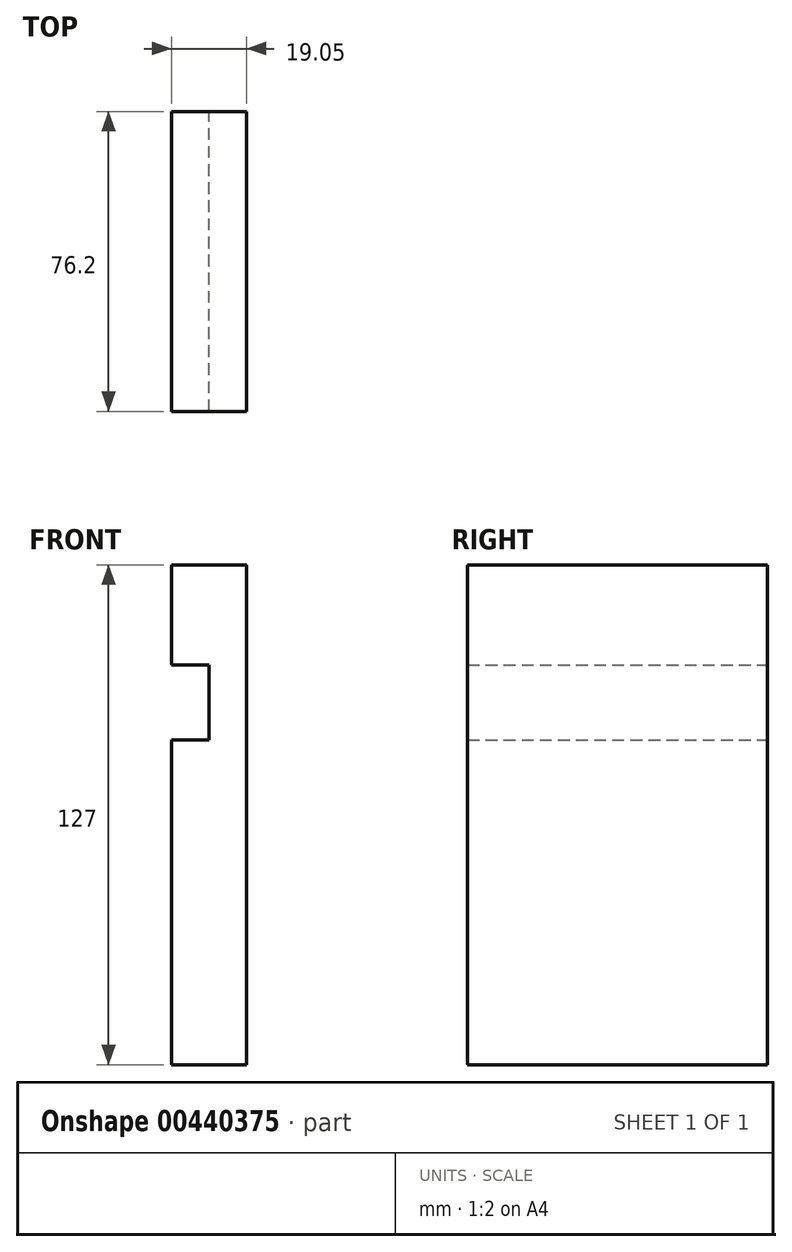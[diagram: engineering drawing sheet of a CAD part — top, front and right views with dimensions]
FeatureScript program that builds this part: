
annotation { "Feature Type Name" : "Feature", "Feature Type Description" : "" }
export const myFeature = defineFeature(function(context is Context, id is Id, definition is map)
    precondition{}
    {
        {
            var Q0;
            Q0=qCreatedBy(makeId("Front.planeOp"),FACE);
            var sketch = newSketch(context, id + "F0", { "sketchPlane" : qUnion([Q0])});
            skLineSegment(sketch, "E0", {"start": v(-28.86, 34.68) * mm, "end": v(-28.86, 161.68) * mm});
            skLineSegment(sketch, "E1", {"start": v(-28.86, 161.68) * mm, "end": v(-47.91, 161.68) * mm});
            skLineSegment(sketch, "E2", {"start": v(-47.91, 161.68) * mm, "end": v(-47.91, 136.28) * mm});
            skLineSegment(sketch, "E3", {"start": v(-47.91, 136.28) * mm, "end": v(-38.39, 136.28) * mm});
            skLineSegment(sketch, "E4", {"start": v(-38.39, 136.28) * mm, "end": v(-38.39, 117.23) * mm});
            skLineSegment(sketch, "E5", {"start": v(-38.39, 117.23) * mm, "end": v(-47.91, 117.23) * mm});
            skLineSegment(sketch, "E6", {"start": v(-47.91, 117.23) * mm, "end": v(-47.91, 34.68) * mm});
            skLineSegment(sketch, "E7", {"start": v(-47.91, 34.68) * mm, "end": v(-28.86, 34.68) * mm});
            skSolve(sketch);
        }
        {
            var Q0;
            Q0 = qSketchRegion(id + "F0", true);
            extrude(context, id + "F1", {"entities" : qUnion([Q0]), "depth" : 76.2 * mm});
        }
    });
